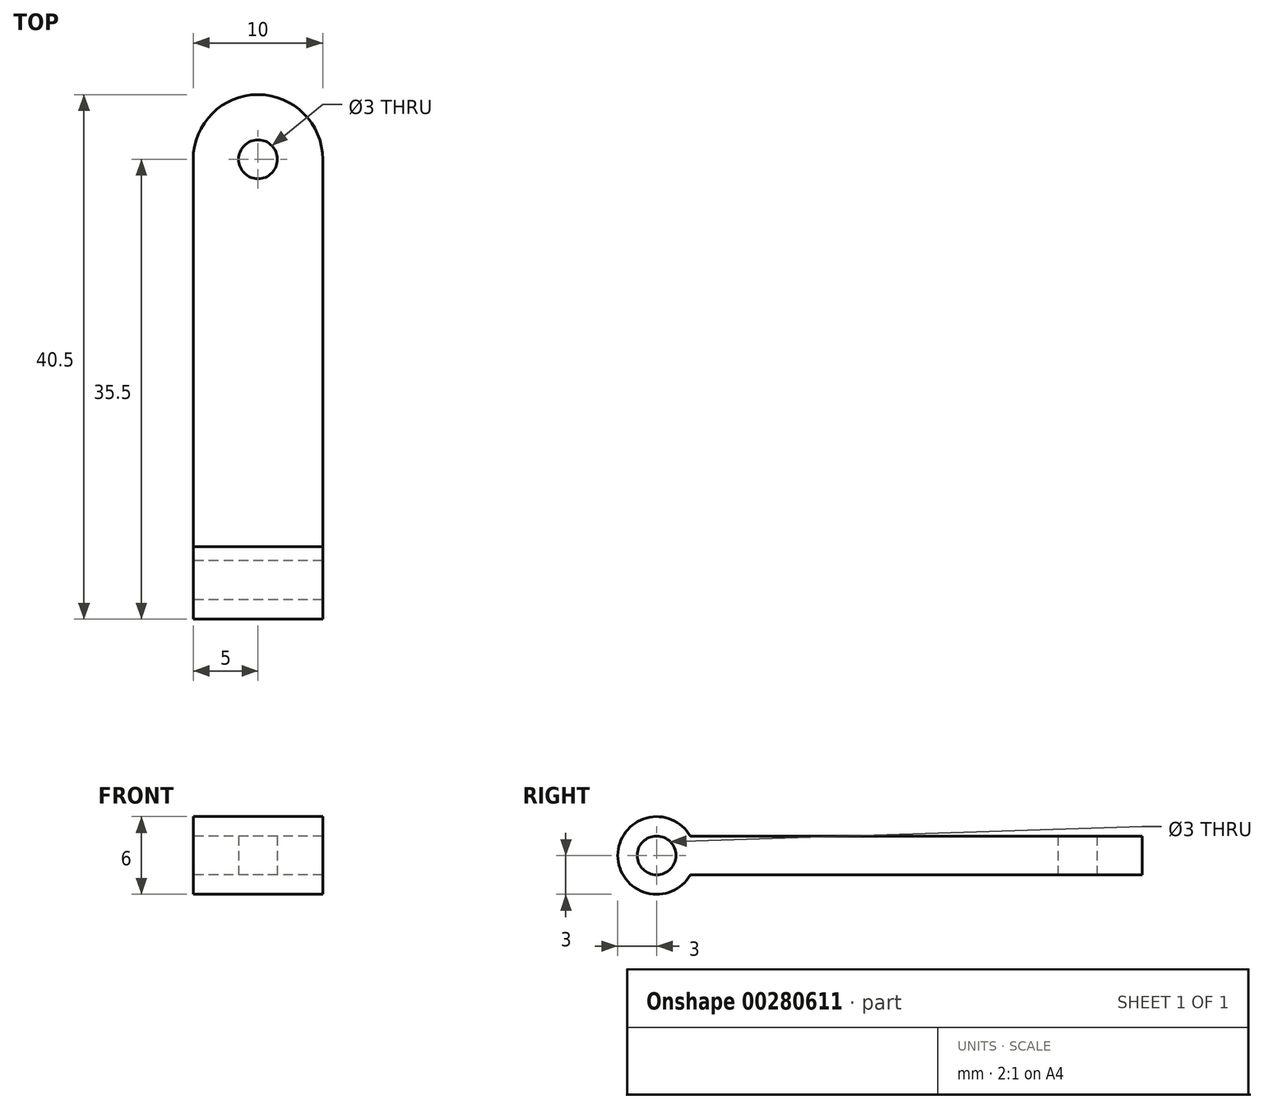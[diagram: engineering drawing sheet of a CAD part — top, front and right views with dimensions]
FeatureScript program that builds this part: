
annotation { "Feature Type Name" : "Feature", "Feature Type Description" : "" }
export const myFeature = defineFeature(function(context is Context, id is Id, definition is map)
    precondition{}
    {
        {
            var Q0;
            Q0=qCreatedBy(makeId("Top.planeOp"),FACE);
            var sketch = newSketch(context, id + "F0", { "sketchPlane" : qUnion([Q0])});
            skLineSegment(sketch, "E0.bottom", {"start": v(5, -17.5) * mm, "end": v(-5, -17.5) * mm});
            skLineSegment(sketch, "E0.left", {"start": v(5, -17.5) * mm, "end": v(5, 17.5) * mm});
            skLineSegment(sketch, "E0.right", {"start": v(-5, -17.5) * mm, "end": v(-5, 17.5) * mm});
            skPoint(sketch, "E0.middle", {"position": v(0, 0) * mm});
            skArc(sketch, "E1", {"start": v(5, 17.5) * mm, "mid": v(0, 22.5) * mm, "end": v(-5, 17.5) * mm});
            skCircle(sketch, "E2", {"center": v(0, 17.5) * mm, "radius": 1.5 * mm});
            skSolve(sketch);
        }
        {
            var Q0;
            Q0=makeQuery(id+"F0.imprint","IMPRINT",FACE,{"disambiguationData":[TD([[makeQuery(id+"F0.imprint","IMPRINT",EDGE,{"derivedFrom":sQuery(id+"F0.wireOp",EDGE,"E0.bottom")}),-1.0]])]});
            extrude(context, id + "F1", {"entities" : qUnion([Q0]), "depth" : 3 * mm});
        }
        {
            var Q0;
            Q0=makeQuery(id+"F1.opExtrude","SWEPT_FACE",FACE,{"disambiguationData":[OSD([sQuery(id+"F0.wireOp",EDGE,"E0.right")])]});
            var sketch = newSketch(context, id + "F2", { "sketchPlane" : qUnion([Q0])});
            skLineSegment(sketch, "E3", {"start": v(17.5, 1.5) * mm, "end": v(15, 1.5) * mm, "construction": true});
            skCircle(sketch, "E4", {"center": v(15, 1.5) * mm, "radius": 1.5 * mm});
            skCircle(sketch, "E5", {"center": v(15, 1.5) * mm, "radius": 3 * mm});
            skSolve(sketch);
        }
        {
            var Q0;
            {var subQ0=sQuery(id+"F0.wireOp",EDGE,"E0.right");var subQ2=makeQuery(id+"F1.opExtrude","SWEPT_EDGE",EDGE,{"disambiguationData":[OSD([sQuery(id+"F0.wireOp",EDGE,"E0.bottom"),subQ0])]});Q0=makeQuery(id+"F2.imprint","IMPRINT",FACE,{"disambiguationData":[TD([[makeQuery(id+"F2.imprint","IMPRINT",EDGE,{"derivedFrom":subQ2}),1.0]])]});}
            var Q1;
            Q1=makeQuery(id+"F1.opExtrude","SWEPT_FACE",FACE,{"disambiguationData":[OSD([sQuery(id+"F0.wireOp",EDGE,"E0.left")])]});
            extrude(context, id + "F3", {"entities" : qUnion([Q0]), "operationType" : NewBodyOperationType.ADD, "endBound" : BoundingType.UP_TO_SURFACE, "oppositeDirection" : true, "endBoundEntityFace" : qUnion([Q1]), "depth" : 25 * mm});
        }
        {
            var Q0;
            {var subQ0=sQuery(id+"F2.wireOp",EDGE,"E4");var subQ1=sQuery(id+"F0.wireOp",EDGE,"E0.right");var subQ2=makeQuery(id+"F2.imprint","INTERSECT",VERTEX,{"derivedFrom":[makeQuery(id+"F1.opExtrude","CAP_EDGE",EDGE,{"disambiguationData":[OSD([subQ1])],"isStart":true}),subQ0]});Q0=makeQuery(id+"F2.imprint","IMPRINT",FACE,{"disambiguationData":[TD([[makeQuery(id+"F2.imprint","IMPRINT",EDGE,{"disambiguationData":[TD([[subQ2,1.0]])],"derivedFrom":subQ0}),1.0]])]});}
            extrude(context, id + "F4", {"entities" : qUnion([Q0]), "operationType" : NewBodyOperationType.REMOVE, "endBound" : BoundingType.THROUGH_ALL, "oppositeDirection" : true, "depth" : 25 * mm});
        }
    });
